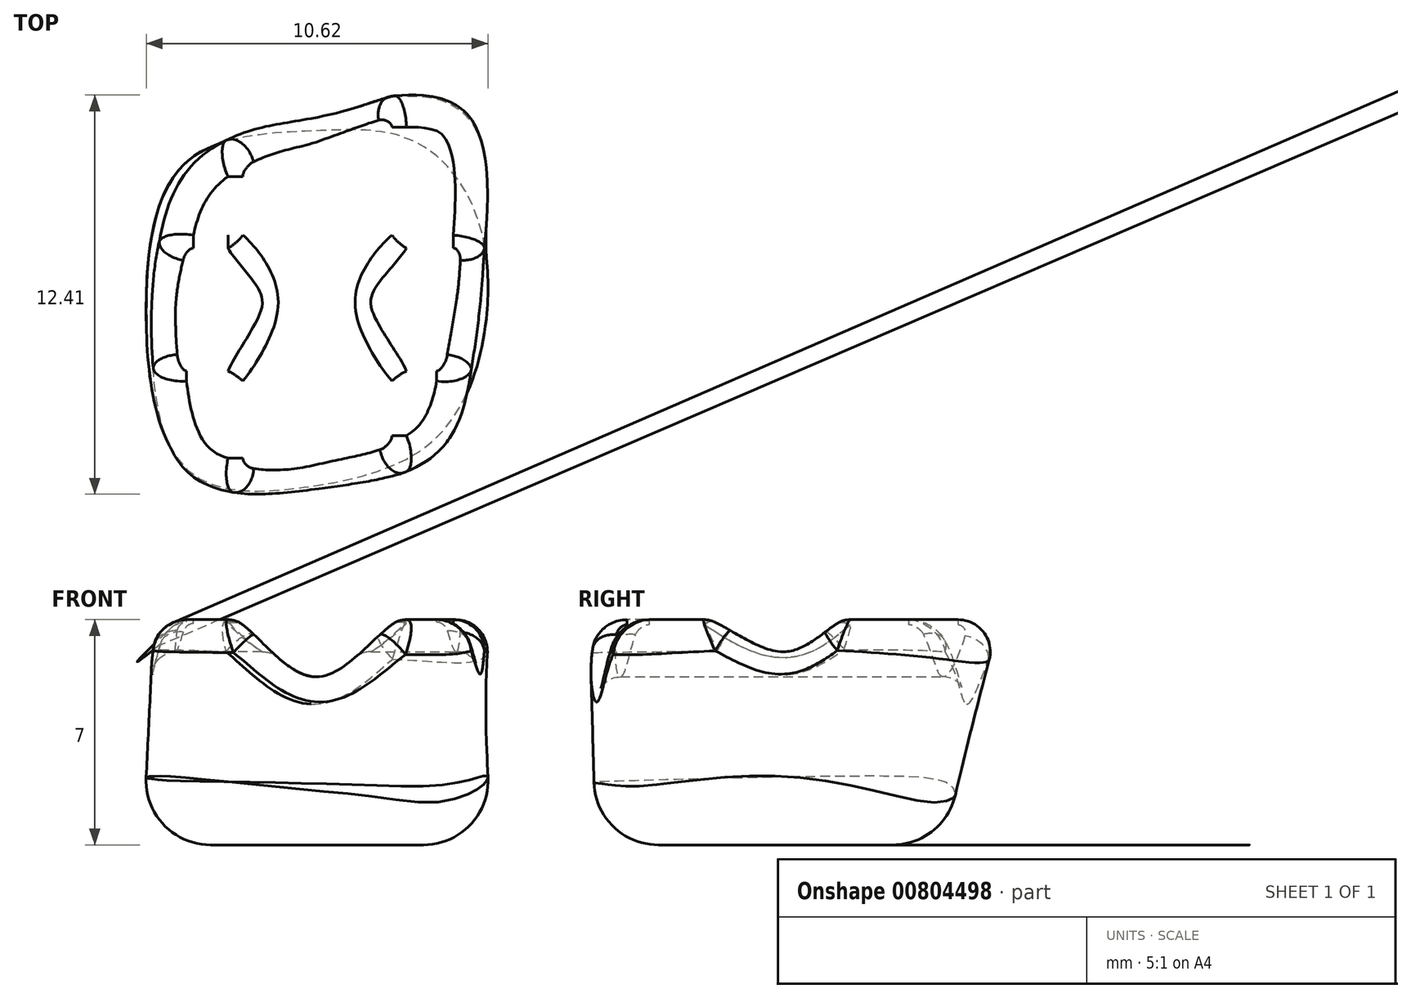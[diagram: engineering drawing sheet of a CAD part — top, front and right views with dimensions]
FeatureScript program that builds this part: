
annotation { "Feature Type Name" : "Feature", "Feature Type Description" : "" }
export const myFeature = defineFeature(function(context is Context, id is Id, definition is map)
    precondition{}
    {
        {
            var Q0;
            Q0=qCreatedBy(makeId("Top.planeOp"),FACE);
            var sketch = newSketch(context, id + "F0", { "sketchPlane" : qUnion([Q0])});
            skLineSegment(sketch, "E0", {"start": v(0, 0) * mm, "end": v(0, 6) * mm, "construction": true});
            skLineSegment(sketch, "E1", {"start": v(0, 0) * mm, "end": v(5, 0) * mm, "construction": true});
            skLineSegment(sketch, "E2", {"start": v(0, 0) * mm, "end": v(0, -6) * mm, "construction": true});
            skLineSegment(sketch, "E3", {"start": v(0, 0) * mm, "end": v(-5, 0) * mm, "construction": true});
            skLineSegment(sketch, "E4", {"start": v(0, 0) * mm, "end": v(-3.86, 4.1) * mm, "construction": true});
            skLineSegment(sketch, "E5", {"start": v(0, 0) * mm, "end": v(4.87, 6.2) * mm, "construction": true});
            skLineSegment(sketch, "E6", {"start": v(0, 0) * mm, "end": v(3.99, -4.68) * mm, "construction": true});
            skLineSegment(sketch, "E7", {"start": v(0, 0) * mm, "end": v(-4.05, -5.3) * mm, "construction": true});
            skFitSpline(sketch, "E8", {"points": [v(-5, 0) * mm, v(-3.86, 4.1) * mm, v(0, 6) * mm, v(4.87, 6.2) * mm, v(5, 0) * mm, v(3.99, -4.68) * mm, v(0, -6) * mm, v(-4.05, -5.3) * mm, v(-5, 0) * mm]});
            skSolve(sketch);
        }
        {
            var Q0;
            Q0=qCreatedBy(makeId("Top.planeOp"),FACE);
            cPlane(context, id + "F1", {"entities" : qUnion([Q0]), "cplaneType" : CPlaneType.OFFSET, "offset" : 7 * mm, "oppositeDirection" : true, "width" : 150 * mm, "height" : 150 * mm});
        }
        {
            var Q0;
            Q0=qCreatedBy(id+"F1.planeOp",FACE);
            var sketch = newSketch(context, id + "F2", { "sketchPlane" : qUnion([Q0])});
            skLineSegment(sketch, "E9", {"start": v(0, 0) * mm, "end": v(0, -5.68) * mm, "construction": true});
            skLineSegment(sketch, "E10", {"start": v(0, 0) * mm, "end": v(5.46, 0) * mm, "construction": true});
            skLineSegment(sketch, "E11", {"start": v(0, 0) * mm, "end": v(0, 4.97) * mm, "construction": true});
            skLineSegment(sketch, "E12", {"start": v(0, 0) * mm, "end": v(-5.38, 0) * mm, "construction": true});
            skLineSegment(sketch, "E13", {"start": v(0, 0) * mm, "end": v(3.26, 4.24) * mm, "construction": true});
            skLineSegment(sketch, "E14", {"start": v(0, 0) * mm, "end": v(-4.07, 4.35) * mm, "construction": true});
            skLineSegment(sketch, "E15", {"start": v(0, 0) * mm, "end": v(-3.91, -5.33) * mm, "construction": true});
            skLineSegment(sketch, "E16", {"start": v(0, 0) * mm, "end": v(3.65, -4.2) * mm, "construction": true});
            skFitSpline(sketch, "E17", {"points": [v(-4.07, 4.35) * mm, v(-5.38, 0) * mm, v(-3.91, -5.33) * mm, v(0, -5.68) * mm, v(3.65, -4.2) * mm, v(5.46, 0) * mm, v(3.26, 4.24) * mm, v(0, 4.97) * mm, v(-4.07, 4.35) * mm]});
            skSolve(sketch);
        }
        {
            var Q0;
            Q0=makeQuery(id+"F0.imprint","IMPRINT",FACE,{"disambiguationData":[TD([[makeQuery(id+"F0.imprint","IMPRINT",EDGE,{"derivedFrom":sQuery(id+"F0.wireOp",EDGE,"E8")}),-1.0]])]});
            var Q1;
            Q1=makeQuery(id+"F2.imprint","IMPRINT",FACE,{"disambiguationData":[TD([[makeQuery(id+"F2.imprint","IMPRINT",EDGE,{"derivedFrom":sQuery(id+"F2.wireOp",EDGE,"E17")}),1.0]])]});
            loft(context, id + "F3", {"sheetProfilesArray" : [{ "sheetProfileEntities" : qUnion([Q0]) }, { "sheetProfileEntities" : qUnion([Q1]) }]});
        }
        {
            var Q0;
            Q0=makeQuery(id+"F3.opLoft","MID_CAP_EDGE",EDGE,{"disambiguationData":[OSD([sQuery(id+"F0.wireOp",EDGE,"E8")])],"capPos":0.0});
            fillet(context, id + "F4", {"entities" : qUnion([Q0]), "radius" : 1 * mm, "tangentPropagation" : true, "allowEdgeOverflow" : false});
        }
        {
            var Q0;
            Q0=makeQuery(id+"F3.opLoft","MID_CAP_EDGE",EDGE,{"disambiguationData":[OSD([sQuery(id+"F2.wireOp",EDGE,"E17")])],"capPos":1.0});
            fillet(context, id + "F5", {"entities" : qUnion([Q0]), "radius" : 2 * mm, "tangentPropagation" : true, "allowEdgeOverflow" : false});
        }
        {
            var Q0;
            Q0=qCreatedBy(makeId("Front.planeOp"),FACE);
            var sketch = newSketch(context, id + "F6", { "sketchPlane" : qUnion([Q0])});
            skLineSegment(sketch, "E18", {"start": v(0, 0) * mm, "end": v(0, -1.78) * mm});
            skLineSegment(sketch, "E19", {"start": v(0, 0) * mm, "end": v(2.6, 0) * mm});
            skLineSegment(sketch, "E20", {"start": v(0, 0) * mm, "end": v(-2.5, 0) * mm});
            skLineSegment(sketch, "E21", {"start": v(-2.5, 0) * mm, "end": v(-3.64, 0) * mm});
            skLineSegment(sketch, "E22", {"start": v(2.6, 0) * mm, "end": v(3.66, 0) * mm});
            skFitSpline(sketch, "E23", {"points": [v(-3.64, 0) * mm, v(-2.5, 0) * mm, v(0, -1.78) * mm, v(2.6, 0) * mm, v(3.66, 0) * mm], "startDerivative": vector(5.66, 1.91) * mm, "endDerivative": vector(5.34, -1.85) * mm});
            skSolve(sketch);
        }
        {
            var Q0;
            Q0 = qSketchRegion(id + "F6", true);
            extrude(context, id + "F7", {"entities" : qUnion([Q0]), "operationType" : NewBodyOperationType.REMOVE, "oppositeDirection" : true, "depth" : 25 * mm, "offsetDistance" : 25 * mm, "hasSecondDirection" : true, "secondDirectionOppositeDirection" : false, "secondDirectionDepth" : 25 * mm});
        }
        {
            var Q0;
            Q0=qCreatedBy(makeId("Right.planeOp"),FACE);
            var sketch = newSketch(context, id + "F8", { "sketchPlane" : qUnion([Q0])});
            skLineSegment(sketch, "E24", {"start": v(0, 0) * mm, "end": v(-2.39, 0) * mm});
            skLineSegment(sketch, "E25", {"start": v(-2.39, 0) * mm, "end": v(-3.4, 0) * mm});
            skLineSegment(sketch, "E26", {"start": v(0, 0) * mm, "end": v(1.81, 0) * mm});
            skLineSegment(sketch, "E27", {"start": v(1.81, 0) * mm, "end": v(2.69, 0) * mm});
            skLineSegment(sketch, "E28", {"start": v(0, 0) * mm, "end": v(0, -1) * mm});
            skFitSpline(sketch, "E29", {"points": [v(2.69, 0) * mm, v(1.81, 0) * mm, v(0, -1) * mm, v(-2.39, 0) * mm, v(-3.4, 0) * mm], "startDerivative": vector(-4.43, 1.15) * mm, "endDerivative": vector(-4.5, -1.1) * mm});
            skSolve(sketch);
        }
        {
            var Q0;
            Q0 = qSketchRegion(id + "F8", true);
            extrude(context, id + "F9", {"entities" : qUnion([Q0]), "operationType" : NewBodyOperationType.REMOVE, "oppositeDirection" : true, "depth" : 25 * mm, "offsetDistance" : 25 * mm, "hasSecondDirection" : true, "secondDirectionOppositeDirection" : false, "secondDirectionDepth" : 25 * mm});
        }
        {
            var Q0;
            {var subQ0=sQuery(id+"F6.wireOp",EDGE,"E23");var subQ1=makeQuery(id+"F6.imprint","INTERSECT",VERTEX,{"derivedFrom":[sQuery(id+"F6.wireOp",EDGE,"E18"),subQ0]});Q0=makeQuery(id+"F7.boolean.opBoolean","INTERSECT",EDGE,{"disambiguationData":[OD(1.0)],"derivedFrom":[makeQuery(id+"F4.opFillet","BLEND_FACE",FACE,{"disambiguationData":[OSD([sQuery(id+"F0.wireOp",EDGE,"E8")])]}),makeQuery(id+"F7.opExtrude","SWEPT_FACE",FACE,{"disambiguationData":[OSD([subQ0]),TDD([makeQuery(id+"F6.imprint","IMPRINT",EDGE,{"disambiguationData":[TD([[subQ1,1.0]])],"derivedFrom":subQ0}),makeQuery(id+"F6.imprint","IMPRINT",EDGE,{"disambiguationData":[TD([[subQ1,-1.0]])],"derivedFrom":subQ0})])]})]});}
            var Q1;
            {var subQ0=sQuery(id+"F6.wireOp",EDGE,"E23");var subQ1=makeQuery(id+"F6.imprint","INTERSECT",VERTEX,{"derivedFrom":[sQuery(id+"F6.wireOp",EDGE,"E18"),subQ0]});Q1=makeQuery(id+"F7.boolean.opBoolean","INTERSECT",EDGE,{"disambiguationData":[OD(1.0)],"derivedFrom":[makeQuery(id+"F3.opLoft","SWEPT_FACE",FACE,{"disambiguationData":[OSD([sQuery(id+"F0.wireOp",EDGE,"E8"),sQuery(id+"F2.wireOp",EDGE,"E17")])]}),makeQuery(id+"F7.opExtrude","SWEPT_FACE",FACE,{"disambiguationData":[OSD([subQ0]),TDD([makeQuery(id+"F6.imprint","IMPRINT",EDGE,{"disambiguationData":[TD([[subQ1,1.0]])],"derivedFrom":subQ0}),makeQuery(id+"F6.imprint","IMPRINT",EDGE,{"disambiguationData":[TD([[subQ1,-1.0]])],"derivedFrom":subQ0})])]})]});}
            var Q2;
            {var subQ0=sQuery(id+"F6.wireOp",EDGE,"E23");var subQ1=makeQuery(id+"F6.imprint","INTERSECT",VERTEX,{"derivedFrom":[sQuery(id+"F6.wireOp",EDGE,"E18"),subQ0]});Q2=makeQuery(id+"F7.boolean.opBoolean","INTERSECT",EDGE,{"disambiguationData":[OD(3.0)],"derivedFrom":[makeQuery(id+"F4.opFillet","BLEND_FACE",FACE,{"disambiguationData":[OSD([sQuery(id+"F0.wireOp",EDGE,"E8")])]}),makeQuery(id+"F7.opExtrude","SWEPT_FACE",FACE,{"disambiguationData":[OSD([subQ0]),TDD([makeQuery(id+"F6.imprint","IMPRINT",EDGE,{"disambiguationData":[TD([[subQ1,1.0]])],"derivedFrom":subQ0}),makeQuery(id+"F6.imprint","IMPRINT",EDGE,{"disambiguationData":[TD([[subQ1,-1.0]])],"derivedFrom":subQ0})])]})]});}
            var Q3;
            {var subQ0=sQuery(id+"F8.wireOp",EDGE,"E29");var subQ1=makeQuery(id+"F8.imprint","INTERSECT",VERTEX,{"derivedFrom":[sQuery(id+"F8.wireOp",EDGE,"E28"),subQ0]});var subQ2=sQuery(id+"F6.wireOp",EDGE,"E23");var subQ3=makeQuery(id+"F6.imprint","INTERSECT",VERTEX,{"derivedFrom":[sQuery(id+"F6.wireOp",EDGE,"E18"),subQ2]});Q3=makeQuery(id+"F9.boolean.opBoolean","INTERSECT",EDGE,{"disambiguationData":[OD(0.0)],"derivedFrom":[makeQuery(id+"F7.boolean.opBoolean","COPY",FACE,{"derivedFrom":makeQuery(id+"F7.opExtrude","SWEPT_FACE",FACE,{"disambiguationData":[OSD([subQ2]),TDD([makeQuery(id+"F6.imprint","IMPRINT",EDGE,{"disambiguationData":[TD([[subQ3,1.0]])],"derivedFrom":subQ2}),makeQuery(id+"F6.imprint","IMPRINT",EDGE,{"disambiguationData":[TD([[subQ3,-1.0]])],"derivedFrom":subQ2})])]})}),makeQuery(id+"F9.opExtrude","SWEPT_FACE",FACE,{"disambiguationData":[OSD([subQ0]),TDD([makeQuery(id+"F8.imprint","IMPRINT",EDGE,{"disambiguationData":[TD([[subQ1,1.0]])],"derivedFrom":subQ0}),makeQuery(id+"F8.imprint","IMPRINT",EDGE,{"disambiguationData":[TD([[subQ1,-1.0]])],"derivedFrom":subQ0})])]})]});}
            var Q4;
            {var subQ0=sQuery(id+"F6.wireOp",EDGE,"E23");var subQ1=makeQuery(id+"F6.imprint","INTERSECT",VERTEX,{"derivedFrom":[sQuery(id+"F6.wireOp",EDGE,"E18"),subQ0]});Q4=makeQuery(id+"F9.boolean.opBoolean","INTERSECT",EDGE,{"disambiguationData":[topologyDisambiguationEdgeConnected([makeQuery(id+"F3.opLoft","CAP_FACE",FACE,{"disambiguationData":[OSD([makeQuery(id+"F0.imprint","IMPRINT",FACE,{"disambiguationData":[TD([[makeQuery(id+"F0.imprint","IMPRINT",EDGE,{"derivedFrom":sQuery(id+"F0.wireOp",EDGE,"E8")}),-1.0]])]})])],"isStart":true}),makeQuery(id+"F7.boolean.opBoolean","COPY",FACE,{"derivedFrom":makeQuery(id+"F7.opExtrude","SWEPT_FACE",FACE,{"disambiguationData":[OSD([subQ0]),TDD([makeQuery(id+"F6.imprint","IMPRINT",EDGE,{"disambiguationData":[TD([[subQ1,1.0]])],"derivedFrom":subQ0}),makeQuery(id+"F6.imprint","IMPRINT",EDGE,{"disambiguationData":[TD([[subQ1,-1.0]])],"derivedFrom":subQ0})])]})})]),OD(0.0)],"derivedFrom":[makeQuery(id+"F9.opExtrude","SWEPT_FACE",FACE,{"disambiguationData":[OSD([sQuery(id+"F8.wireOp",EDGE,"E25")])]}),makeQuery(id+"F9.opExtrude","SWEPT_FACE",FACE,{"disambiguationData":[OSD([sQuery(id+"F8.wireOp",EDGE,"E27")])]})]});}
            var Q5;
            {var subQ0=sQuery(id+"F6.wireOp",EDGE,"E23");var subQ1=makeQuery(id+"F6.imprint","INTERSECT",VERTEX,{"derivedFrom":[sQuery(id+"F6.wireOp",EDGE,"E18"),subQ0]});Q5=makeQuery(id+"F7.boolean.opBoolean","INTERSECT",EDGE,{"disambiguationData":[OD(0.0)],"derivedFrom":[makeQuery(id+"F4.opFillet","BLEND_FACE",FACE,{"disambiguationData":[OSD([sQuery(id+"F0.wireOp",EDGE,"E8")])]}),makeQuery(id+"F7.opExtrude","SWEPT_FACE",FACE,{"disambiguationData":[OSD([subQ0]),TDD([makeQuery(id+"F6.imprint","IMPRINT",EDGE,{"disambiguationData":[TD([[subQ1,1.0]])],"derivedFrom":subQ0}),makeQuery(id+"F6.imprint","IMPRINT",EDGE,{"disambiguationData":[TD([[subQ1,-1.0]])],"derivedFrom":subQ0})])]})]});}
            var Q6;
            {var subQ0=sQuery(id+"F6.wireOp",EDGE,"E23");var subQ1=makeQuery(id+"F6.imprint","INTERSECT",VERTEX,{"derivedFrom":[sQuery(id+"F6.wireOp",EDGE,"E18"),subQ0]});Q6=makeQuery(id+"F7.boolean.opBoolean","INTERSECT",EDGE,{"disambiguationData":[OD(0.0)],"derivedFrom":[makeQuery(id+"F3.opLoft","SWEPT_FACE",FACE,{"disambiguationData":[OSD([sQuery(id+"F0.wireOp",EDGE,"E8"),sQuery(id+"F2.wireOp",EDGE,"E17")])]}),makeQuery(id+"F7.opExtrude","SWEPT_FACE",FACE,{"disambiguationData":[OSD([subQ0]),TDD([makeQuery(id+"F6.imprint","IMPRINT",EDGE,{"disambiguationData":[TD([[subQ1,1.0]])],"derivedFrom":subQ0}),makeQuery(id+"F6.imprint","IMPRINT",EDGE,{"disambiguationData":[TD([[subQ1,-1.0]])],"derivedFrom":subQ0})])]})]});}
            var Q7;
            {var subQ0=sQuery(id+"F6.wireOp",EDGE,"E23");var subQ1=makeQuery(id+"F6.imprint","INTERSECT",VERTEX,{"derivedFrom":[sQuery(id+"F6.wireOp",EDGE,"E18"),subQ0]});Q7=makeQuery(id+"F7.boolean.opBoolean","INTERSECT",EDGE,{"disambiguationData":[OD(2.0)],"derivedFrom":[makeQuery(id+"F4.opFillet","BLEND_FACE",FACE,{"disambiguationData":[OSD([sQuery(id+"F0.wireOp",EDGE,"E8")])]}),makeQuery(id+"F7.opExtrude","SWEPT_FACE",FACE,{"disambiguationData":[OSD([subQ0]),TDD([makeQuery(id+"F6.imprint","IMPRINT",EDGE,{"disambiguationData":[TD([[subQ1,1.0]])],"derivedFrom":subQ0}),makeQuery(id+"F6.imprint","IMPRINT",EDGE,{"disambiguationData":[TD([[subQ1,-1.0]])],"derivedFrom":subQ0})])]})]});}
            var Q8;
            {var subQ0=sQuery(id+"F6.wireOp",EDGE,"E23");var subQ1=makeQuery(id+"F6.imprint","INTERSECT",VERTEX,{"derivedFrom":[sQuery(id+"F6.wireOp",EDGE,"E18"),subQ0]});Q8=makeQuery(id+"F9.boolean.opBoolean","INTERSECT",EDGE,{"disambiguationData":[topologyDisambiguationEdgeConnected([makeQuery(id+"F3.opLoft","CAP_FACE",FACE,{"disambiguationData":[OSD([makeQuery(id+"F0.imprint","IMPRINT",FACE,{"disambiguationData":[TD([[makeQuery(id+"F0.imprint","IMPRINT",EDGE,{"derivedFrom":sQuery(id+"F0.wireOp",EDGE,"E8")}),-1.0]])]})])],"isStart":true}),makeQuery(id+"F7.boolean.opBoolean","COPY",FACE,{"derivedFrom":makeQuery(id+"F7.opExtrude","SWEPT_FACE",FACE,{"disambiguationData":[OSD([subQ0]),TDD([makeQuery(id+"F6.imprint","IMPRINT",EDGE,{"disambiguationData":[TD([[subQ1,1.0]])],"derivedFrom":subQ0}),makeQuery(id+"F6.imprint","IMPRINT",EDGE,{"disambiguationData":[TD([[subQ1,-1.0]])],"derivedFrom":subQ0})])]})})]),OD(2.0)],"derivedFrom":[makeQuery(id+"F9.opExtrude","SWEPT_FACE",FACE,{"disambiguationData":[OSD([sQuery(id+"F8.wireOp",EDGE,"E25")])]}),makeQuery(id+"F9.opExtrude","SWEPT_FACE",FACE,{"disambiguationData":[OSD([sQuery(id+"F8.wireOp",EDGE,"E27")])]})]});}
            var Q9;
            {var subQ0=sQuery(id+"F8.wireOp",EDGE,"E29");var subQ1=makeQuery(id+"F8.imprint","INTERSECT",VERTEX,{"derivedFrom":[sQuery(id+"F8.wireOp",EDGE,"E28"),subQ0]});var subQ2=sQuery(id+"F6.wireOp",EDGE,"E23");var subQ3=makeQuery(id+"F6.imprint","INTERSECT",VERTEX,{"derivedFrom":[sQuery(id+"F6.wireOp",EDGE,"E18"),subQ2]});Q9=makeQuery(id+"F9.boolean.opBoolean","INTERSECT",EDGE,{"disambiguationData":[OD(1.0)],"derivedFrom":[makeQuery(id+"F7.boolean.opBoolean","COPY",FACE,{"derivedFrom":makeQuery(id+"F7.opExtrude","SWEPT_FACE",FACE,{"disambiguationData":[OSD([subQ2]),TDD([makeQuery(id+"F6.imprint","IMPRINT",EDGE,{"disambiguationData":[TD([[subQ3,1.0]])],"derivedFrom":subQ2}),makeQuery(id+"F6.imprint","IMPRINT",EDGE,{"disambiguationData":[TD([[subQ3,-1.0]])],"derivedFrom":subQ2})])]})}),makeQuery(id+"F9.opExtrude","SWEPT_FACE",FACE,{"disambiguationData":[OSD([subQ0]),TDD([makeQuery(id+"F8.imprint","IMPRINT",EDGE,{"disambiguationData":[TD([[subQ1,1.0]])],"derivedFrom":subQ0}),makeQuery(id+"F8.imprint","IMPRINT",EDGE,{"disambiguationData":[TD([[subQ1,-1.0]])],"derivedFrom":subQ0})])]})]});}
            var Q10;
            {var subQ0=sQuery(id+"F6.wireOp",EDGE,"E23");var subQ1=makeQuery(id+"F6.imprint","INTERSECT",VERTEX,{"derivedFrom":[sQuery(id+"F6.wireOp",EDGE,"E18"),subQ0]});Q10=makeQuery(id+"F9.boolean.opBoolean","INTERSECT",EDGE,{"disambiguationData":[topologyDisambiguationEdgeConnected([makeQuery(id+"F3.opLoft","CAP_FACE",FACE,{"disambiguationData":[OSD([makeQuery(id+"F0.imprint","IMPRINT",FACE,{"disambiguationData":[TD([[makeQuery(id+"F0.imprint","IMPRINT",EDGE,{"derivedFrom":sQuery(id+"F0.wireOp",EDGE,"E8")}),-1.0]])]})])],"isStart":true}),makeQuery(id+"F7.boolean.opBoolean","COPY",FACE,{"derivedFrom":makeQuery(id+"F7.opExtrude","SWEPT_FACE",FACE,{"disambiguationData":[OSD([subQ0]),TDD([makeQuery(id+"F6.imprint","IMPRINT",EDGE,{"disambiguationData":[TD([[subQ1,1.0]])],"derivedFrom":subQ0}),makeQuery(id+"F6.imprint","IMPRINT",EDGE,{"disambiguationData":[TD([[subQ1,-1.0]])],"derivedFrom":subQ0})])]})})]),OD(3.0)],"derivedFrom":[makeQuery(id+"F9.opExtrude","SWEPT_FACE",FACE,{"disambiguationData":[OSD([sQuery(id+"F8.wireOp",EDGE,"E25")])]}),makeQuery(id+"F9.opExtrude","SWEPT_FACE",FACE,{"disambiguationData":[OSD([sQuery(id+"F8.wireOp",EDGE,"E27")])]})]});}
            fillet(context, id + "F10", {"entities" : qUnion([Q0, Q1, Q2, Q3, Q4, Q5, Q6, Q7, Q8, Q9, Q10]), "radius" : 0.75 * mm, "tangentPropagation" : true, "allowEdgeOverflow" : false});
        }
        {
            var Q0;
            Q0=makeQuery(id+"F9.boolean.opBoolean","COPY",EDGE,{"disambiguationData":[OD(0.0)],"derivedFrom":makeQuery(id+"F9.opExtrude","SWEPT_EDGE",EDGE,{"disambiguationData":[OSD([sQuery(id+"F8.wireOp",EDGE,"E24"),sQuery(id+"F8.wireOp",EDGE,"E25"),sQuery(id+"F8.wireOp",EDGE,"E29")]),OD(0.0)]})});
            var Q1;
            {var subQ0=sQuery(id+"F8.wireOp",EDGE,"E29");var subQ1=makeQuery(id+"F8.imprint","INTERSECT",VERTEX,{"derivedFrom":[sQuery(id+"F8.wireOp",EDGE,"E28"),subQ0]});Q1=makeQuery(id+"F9.boolean.opBoolean","INTERSECT",EDGE,{"disambiguationData":[OD(0.0)],"derivedFrom":[makeQuery(id+"F7.boolean.opBoolean","SPLIT",FACE,{"disambiguationData":[OD(0.0)],"derivedFrom":makeQuery(id+"F4.opFillet","BLEND_FACE",FACE,{"disambiguationData":[OSD([sQuery(id+"F0.wireOp",EDGE,"E8")])]})}),makeQuery(id+"F9.opExtrude","SWEPT_FACE",FACE,{"disambiguationData":[OSD([subQ0]),TDD([makeQuery(id+"F8.imprint","IMPRINT",EDGE,{"disambiguationData":[TD([[subQ1,1.0]])],"derivedFrom":subQ0}),makeQuery(id+"F8.imprint","IMPRINT",EDGE,{"disambiguationData":[TD([[subQ1,-1.0]])],"derivedFrom":subQ0})])]})]});}
            var Q2;
            {var subQ0=sQuery(id+"F8.wireOp",EDGE,"E29");var subQ1=makeQuery(id+"F8.imprint","INTERSECT",VERTEX,{"derivedFrom":[sQuery(id+"F8.wireOp",EDGE,"E28"),subQ0]});Q2=makeQuery(id+"F9.boolean.opBoolean","INTERSECT",EDGE,{"disambiguationData":[OD(0.0)],"derivedFrom":[makeQuery(id+"F3.opLoft","SWEPT_FACE",FACE,{"disambiguationData":[OSD([sQuery(id+"F0.wireOp",EDGE,"E8"),sQuery(id+"F2.wireOp",EDGE,"E17")])]}),makeQuery(id+"F9.opExtrude","SWEPT_FACE",FACE,{"disambiguationData":[OSD([subQ0]),TDD([makeQuery(id+"F8.imprint","IMPRINT",EDGE,{"disambiguationData":[TD([[subQ1,1.0]])],"derivedFrom":subQ0}),makeQuery(id+"F8.imprint","IMPRINT",EDGE,{"disambiguationData":[TD([[subQ1,-1.0]])],"derivedFrom":subQ0})])]})]});}
            var Q3;
            {var subQ0=sQuery(id+"F8.wireOp",EDGE,"E29");var subQ1=makeQuery(id+"F8.imprint","INTERSECT",VERTEX,{"derivedFrom":[sQuery(id+"F8.wireOp",EDGE,"E28"),subQ0]});Q3=makeQuery(id+"F9.boolean.opBoolean","INTERSECT",EDGE,{"disambiguationData":[OD(1.0)],"derivedFrom":[makeQuery(id+"F7.boolean.opBoolean","SPLIT",FACE,{"disambiguationData":[OD(0.0)],"derivedFrom":makeQuery(id+"F4.opFillet","BLEND_FACE",FACE,{"disambiguationData":[OSD([sQuery(id+"F0.wireOp",EDGE,"E8")])]})}),makeQuery(id+"F9.opExtrude","SWEPT_FACE",FACE,{"disambiguationData":[OSD([subQ0]),TDD([makeQuery(id+"F8.imprint","IMPRINT",EDGE,{"disambiguationData":[TD([[subQ1,1.0]])],"derivedFrom":subQ0}),makeQuery(id+"F8.imprint","IMPRINT",EDGE,{"disambiguationData":[TD([[subQ1,-1.0]])],"derivedFrom":subQ0})])]})]});}
            var Q4;
            Q4=makeQuery(id+"F9.boolean.opBoolean","COPY",EDGE,{"disambiguationData":[OD(0.0)],"derivedFrom":makeQuery(id+"F9.opExtrude","SWEPT_EDGE",EDGE,{"disambiguationData":[OSD([sQuery(id+"F8.wireOp",EDGE,"E26"),sQuery(id+"F8.wireOp",EDGE,"E27"),sQuery(id+"F8.wireOp",EDGE,"E29")]),OD(0.0)]})});
            var Q5;
            Q5=makeQuery(id+"F9.boolean.opBoolean","COPY",EDGE,{"disambiguationData":[OD(1.0)],"derivedFrom":makeQuery(id+"F9.opExtrude","SWEPT_EDGE",EDGE,{"disambiguationData":[OSD([sQuery(id+"F8.wireOp",EDGE,"E24"),sQuery(id+"F8.wireOp",EDGE,"E25"),sQuery(id+"F8.wireOp",EDGE,"E29")]),OD(0.0)]})});
            var Q6;
            {var subQ0=sQuery(id+"F8.wireOp",EDGE,"E29");var subQ1=makeQuery(id+"F8.imprint","INTERSECT",VERTEX,{"derivedFrom":[sQuery(id+"F8.wireOp",EDGE,"E28"),subQ0]});Q6=makeQuery(id+"F9.boolean.opBoolean","INTERSECT",EDGE,{"disambiguationData":[OD(0.0)],"derivedFrom":[makeQuery(id+"F7.boolean.opBoolean","SPLIT",FACE,{"disambiguationData":[OD(1.0)],"derivedFrom":makeQuery(id+"F4.opFillet","BLEND_FACE",FACE,{"disambiguationData":[OSD([sQuery(id+"F0.wireOp",EDGE,"E8")])]})}),makeQuery(id+"F9.opExtrude","SWEPT_FACE",FACE,{"disambiguationData":[OSD([subQ0]),TDD([makeQuery(id+"F8.imprint","IMPRINT",EDGE,{"disambiguationData":[TD([[subQ1,1.0]])],"derivedFrom":subQ0}),makeQuery(id+"F8.imprint","IMPRINT",EDGE,{"disambiguationData":[TD([[subQ1,-1.0]])],"derivedFrom":subQ0})])]})]});}
            var Q7;
            {var subQ0=sQuery(id+"F8.wireOp",EDGE,"E29");var subQ1=makeQuery(id+"F8.imprint","INTERSECT",VERTEX,{"derivedFrom":[sQuery(id+"F8.wireOp",EDGE,"E28"),subQ0]});Q7=makeQuery(id+"F9.boolean.opBoolean","INTERSECT",EDGE,{"disambiguationData":[OD(1.0)],"derivedFrom":[makeQuery(id+"F3.opLoft","SWEPT_FACE",FACE,{"disambiguationData":[OSD([sQuery(id+"F0.wireOp",EDGE,"E8"),sQuery(id+"F2.wireOp",EDGE,"E17")])]}),makeQuery(id+"F9.opExtrude","SWEPT_FACE",FACE,{"disambiguationData":[OSD([subQ0]),TDD([makeQuery(id+"F8.imprint","IMPRINT",EDGE,{"disambiguationData":[TD([[subQ1,1.0]])],"derivedFrom":subQ0}),makeQuery(id+"F8.imprint","IMPRINT",EDGE,{"disambiguationData":[TD([[subQ1,-1.0]])],"derivedFrom":subQ0})])]})]});}
            var Q8;
            {var subQ0=sQuery(id+"F8.wireOp",EDGE,"E29");var subQ1=makeQuery(id+"F8.imprint","INTERSECT",VERTEX,{"derivedFrom":[sQuery(id+"F8.wireOp",EDGE,"E28"),subQ0]});Q8=makeQuery(id+"F9.boolean.opBoolean","INTERSECT",EDGE,{"disambiguationData":[OD(1.0)],"derivedFrom":[makeQuery(id+"F7.boolean.opBoolean","SPLIT",FACE,{"disambiguationData":[OD(1.0)],"derivedFrom":makeQuery(id+"F4.opFillet","BLEND_FACE",FACE,{"disambiguationData":[OSD([sQuery(id+"F0.wireOp",EDGE,"E8")])]})}),makeQuery(id+"F9.opExtrude","SWEPT_FACE",FACE,{"disambiguationData":[OSD([subQ0]),TDD([makeQuery(id+"F8.imprint","IMPRINT",EDGE,{"disambiguationData":[TD([[subQ1,1.0]])],"derivedFrom":subQ0}),makeQuery(id+"F8.imprint","IMPRINT",EDGE,{"disambiguationData":[TD([[subQ1,-1.0]])],"derivedFrom":subQ0})])]})]});}
            var Q9;
            Q9=makeQuery(id+"F9.boolean.opBoolean","COPY",EDGE,{"disambiguationData":[OD(1.0)],"derivedFrom":makeQuery(id+"F9.opExtrude","SWEPT_EDGE",EDGE,{"disambiguationData":[OSD([sQuery(id+"F8.wireOp",EDGE,"E26"),sQuery(id+"F8.wireOp",EDGE,"E27"),sQuery(id+"F8.wireOp",EDGE,"E29")]),OD(0.0)]})});
            fillet(context, id + "F11", {"entities" : qUnion([Q0, Q1, Q2, Q3, Q4, Q5, Q6, Q7, Q8, Q9]), "radius" : 0.75 * mm, "tangentPropagation" : true, "allowEdgeOverflow" : false});
        }
    });
